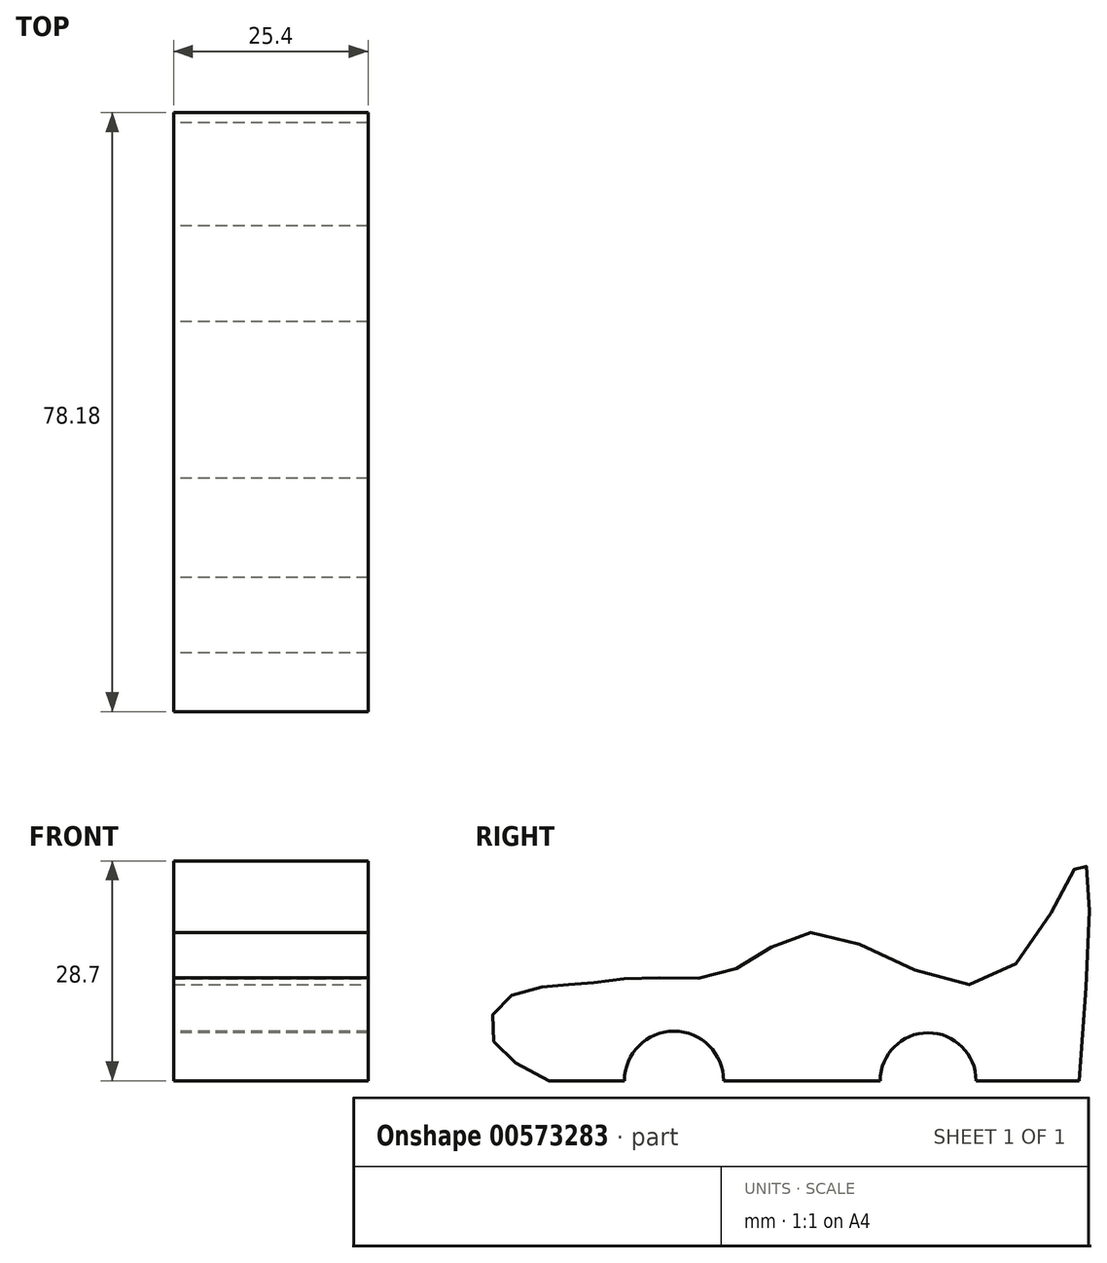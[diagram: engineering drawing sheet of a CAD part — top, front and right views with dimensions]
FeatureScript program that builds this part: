
annotation { "Feature Type Name" : "Feature", "Feature Type Description" : "" }
export const myFeature = defineFeature(function(context is Context, id is Id, definition is map)
    precondition{}
    {
        {
            var Q0;
            Q0=qCreatedBy(makeId("Right.planeOp"),FACE);
            var sketch = newSketch(context, id + "F0", { "sketchPlane" : qUnion([Q0])});
            skFitSpline(sketch, "E0", {"points": [v(0, 0) * mm, v(-7.2, 5.12) * mm, v(-6.45, 10.05) * mm, v(0, 12.32) * mm, v(4.93, 12.7) * mm, v(12.32, 13.46) * mm, v(23.51, 14.22) * mm, v(35.45, 19.34) * mm, v(57.83, 13.08) * mm, v(69.4, 28.63) * mm, v(69.2, 0) * mm], "startDerivative": vector(-105.97, 51.14) * mm, "endDerivative": vector(-21.52, -287.2) * mm});
            skLineSegment(sketch, "E1", {"start": v(0, 0) * mm, "end": v(69.2, 0) * mm});
            skCircle(sketch, "E2", {"center": v(16.3, 0) * mm, "radius": 6.47 * mm});
            skCircle(sketch, "E3", {"center": v(49.48, 0) * mm, "radius": 6.26 * mm});
            skSolve(sketch);
        }
        {
            var Q0;
            {var subQ5=sQuery(id+"F0.wireOp",EDGE,"E0");Q0=makeQuery(id+"F0.imprint","IMPRINT",FACE,{"disambiguationData":[TD([[makeQuery(id+"F0.imprint","IMPRINT",EDGE,{"derivedFrom":subQ5}),-1.0]])]});}
            extrude(context, id + "F1", {"entities" : qUnion([Q0]), "depth" : 25.4 * mm, "offsetDistance" : 25.4 * mm});
        }
    });
